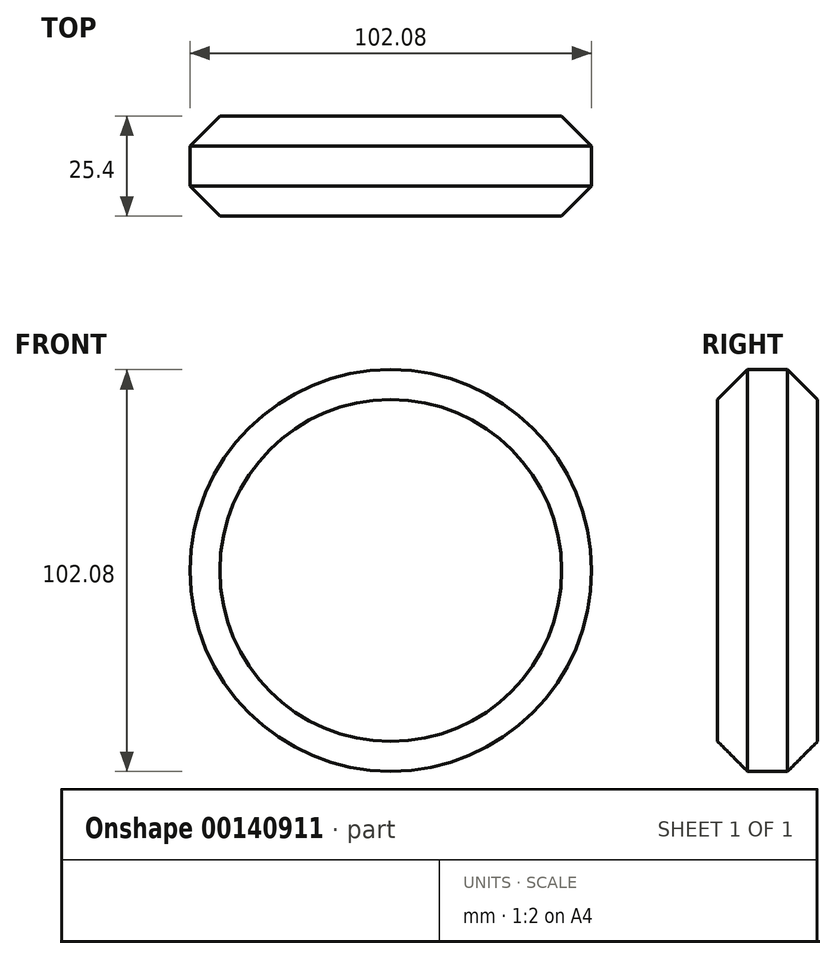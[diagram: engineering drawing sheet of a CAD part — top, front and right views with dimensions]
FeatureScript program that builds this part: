
annotation { "Feature Type Name" : "Feature", "Feature Type Description" : "" }
export const myFeature = defineFeature(function(context is Context, id is Id, definition is map)
    precondition{}
    {
        {
            var Q0;
            Q0=qCreatedBy(makeId("Front.planeOp"),FACE);
            var sketch = newSketch(context, id + "F0", { "sketchPlane" : qUnion([Q0])});
            skCircle(sketch, "E0", {"center": v(0, 0) * mm, "radius": 51.04 * mm});
            skSolve(sketch);
        }
        {
            var Q0;
            Q0 = qSketchRegion(id + "F0", true);
            extrude(context, id + "F1", {"entities" : qUnion([Q0]), "depth" : 25.4 * mm});
        }
        {
            var Q0;
            Q0=makeQuery(id+"F1.opExtrude","CAP_FACE",FACE,{"disambiguationData":[OSD([sQuery(id+"F0.wireOp",EDGE,"E0")])],"isStart":false});
            var Q1;
            Q1=makeQuery(id+"F1.opExtrude","CAP_FACE",FACE,{"disambiguationData":[OSD([sQuery(id+"F0.wireOp",EDGE,"E0")])],"isStart":true});
            chamfer(context, id + "F2", {"entities" : qUnion([Q0, Q1]), "width" : 7.62 * mm, "tangentPropagation" : true});
        }
    });
